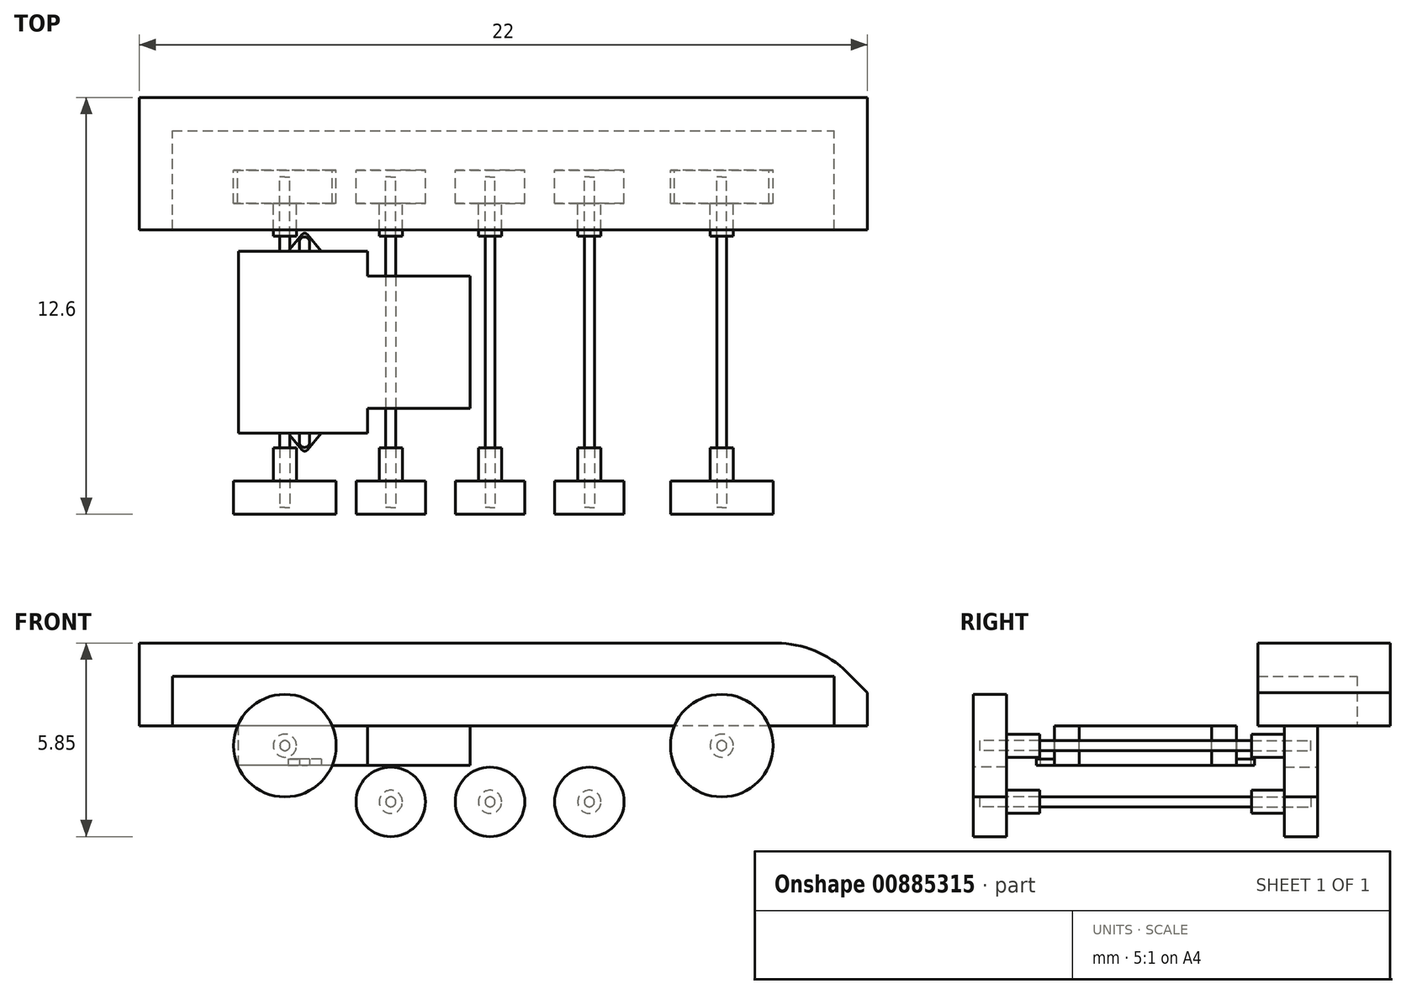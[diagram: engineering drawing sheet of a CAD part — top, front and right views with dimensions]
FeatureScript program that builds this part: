
annotation { "Feature Type Name" : "Feature", "Feature Type Description" : "" }
export const myFeature = defineFeature(function(context is Context, id is Id, definition is map)
    precondition{}
    {
        {
            var Q0;
            Q0=qCreatedBy(makeId("Front.planeOp"),FACE);
            var sketch = newSketch(context, id + "F0", { "sketchPlane" : qUnion([Q0])});
            skCircle(sketch, "E0", {"center": v(-6.6, 0) * mm, "radius": 0.15 * mm});
            skCircle(sketch, "E1", {"center": v(6.6, 0) * mm, "radius": 0.15 * mm});
            skCircle(sketch, "E2", {"center": v(-3.4, -1.7) * mm, "radius": 0.15 * mm});
            skCircle(sketch, "E3", {"center": v(-0.4, -1.7) * mm, "radius": 0.15 * mm});
            skCircle(sketch, "E4", {"center": v(2.6, -1.7) * mm, "radius": 0.15 * mm});
            skSolve(sketch);
        }
        {
            var Q0;
            Q0=makeQuery(id+"F0.imprint","IMPRINT",FACE,{"disambiguationData":[TD([[makeQuery(id+"F0.imprint","IMPRINT",EDGE,{"derivedFrom":sQuery(id+"F0.wireOp",EDGE,"E0")}),1.0]])]});
            var Q1;
            Q1=makeQuery(id+"F0.imprint","IMPRINT",FACE,{"disambiguationData":[TD([[makeQuery(id+"F0.imprint","IMPRINT",EDGE,{"derivedFrom":sQuery(id+"F0.wireOp",EDGE,"E1")}),1.0]])]});
            var Q2;
            Q2=makeQuery(id+"F0.imprint","IMPRINT",FACE,{"disambiguationData":[TD([[makeQuery(id+"F0.imprint","IMPRINT",EDGE,{"derivedFrom":sQuery(id+"F0.wireOp",EDGE,"E2")}),1.0]])]});
            var Q3;
            Q3=makeQuery(id+"F0.imprint","IMPRINT",FACE,{"disambiguationData":[TD([[makeQuery(id+"F0.imprint","IMPRINT",EDGE,{"derivedFrom":sQuery(id+"F0.wireOp",EDGE,"E3")}),1.0]])]});
            var Q4;
            Q4=makeQuery(id+"F0.imprint","IMPRINT",FACE,{"disambiguationData":[TD([[makeQuery(id+"F0.imprint","IMPRINT",EDGE,{"derivedFrom":sQuery(id+"F0.wireOp",EDGE,"E4")}),1.0]])]});
            extrude(context, id + "F1", {"entities" : qUnion([Q0, Q1, Q2, Q3, Q4]), "endBound" : BoundingType.SYMMETRIC, "depth" : 10 * mm, "offsetDistance" : 25 * mm});
        }
        {
            var Q0;
            Q0=makeQuery(id+"F1.opExtrude","CAP_FACE",FACE,{"disambiguationData":[OSD([sQuery(id+"F0.wireOp",EDGE,"E1")])],"isStart":false});
            var sketch = newSketch(context, id + "F2", { "sketchPlane" : qUnion([Q0])});
            skCircle(sketch, "E5", {"center": v(6.6, 0) * mm, "radius": 1.55 * mm});
            skPoint(sketch, "E6", {"position": v(2.6, -1.7) * mm});
            skPoint(sketch, "E7", {"position": v(-0.4, -1.7) * mm});
            skPoint(sketch, "E8", {"position": v(-3.4, -1.7) * mm});
            skPoint(sketch, "E9", {"position": v(-6.6, 0) * mm});
            skCircle(sketch, "E10", {"center": v(-6.6, 0) * mm, "radius": 1.55 * mm});
            skCircle(sketch, "E11", {"center": v(-3.4, -1.7) * mm, "radius": 1.05 * mm});
            skCircle(sketch, "E12", {"center": v(-0.4, -1.7) * mm, "radius": 1.05 * mm});
            skCircle(sketch, "E13", {"center": v(2.6, -1.7) * mm, "radius": 1.05 * mm});
            skSolve(sketch);
        }
        {
            var Q0;
            Q0=makeQuery(id+"F2.imprint","IMPRINT",FACE,{"disambiguationData":[TD([[makeQuery(id+"F2.imprint","IMPRINT",EDGE,{"derivedFrom":sQuery(id+"F2.wireOp",EDGE,"E10")}),1.0]])]});
            var Q1;
            Q1=makeQuery(id+"F2.imprint","IMPRINT",FACE,{"disambiguationData":[TD([[makeQuery(id+"F2.imprint","IMPRINT",EDGE,{"derivedFrom":sQuery(id+"F2.wireOp",EDGE,"E11")}),1.0]])]});
            var Q2;
            Q2=makeQuery(id+"F2.imprint","IMPRINT",FACE,{"disambiguationData":[TD([[makeQuery(id+"F2.imprint","IMPRINT",EDGE,{"derivedFrom":sQuery(id+"F2.wireOp",EDGE,"E12")}),1.0]])]});
            var Q3;
            Q3=makeQuery(id+"F2.imprint","IMPRINT",FACE,{"disambiguationData":[TD([[makeQuery(id+"F2.imprint","IMPRINT",EDGE,{"derivedFrom":sQuery(id+"F2.wireOp",EDGE,"E13")}),1.0]])]});
            var Q4;
            Q4=makeQuery(id+"F2.imprint","IMPRINT",FACE,{"disambiguationData":[TD([[makeQuery(id+"F2.imprint","IMPRINT",EDGE,{"derivedFrom":sQuery(id+"F2.wireOp",EDGE,"E5")}),1.0]])]});
            extrude(context, id + "F3", {"entities" : qUnion([Q0, Q1, Q2, Q3, Q4]), "oppositeDirection" : true, "depth" : .8 * mm, "offsetDistance" : 25 * mm});
        }
        {
            var Q0;
            Q0=makeQuery(id+"F3.opExtrude","CAP_FACE",FACE,{"disambiguationData":[OSD([sQuery(id+"F2.wireOp",EDGE,"E10")])],"isStart":false});
            var sketch = newSketch(context, id + "F4", { "sketchPlane" : qUnion([Q0])});
            skCircle(sketch, "E14", {"center": v(6.6, 0) * mm, "radius": 0.35 * mm});
            skPoint(sketch, "E15", {"position": v(3.4, -1.7) * mm});
            skPoint(sketch, "E16", {"position": v(0.4, -1.7) * mm});
            skPoint(sketch, "E17", {"position": v(-2.6, -1.7) * mm});
            skPoint(sketch, "E18", {"position": v(-6.6, 0) * mm});
            skCircle(sketch, "E19", {"center": v(3.4, -1.7) * mm, "radius": 0.35 * mm});
            skCircle(sketch, "E20", {"center": v(0.4, -1.7) * mm, "radius": 0.35 * mm});
            skCircle(sketch, "E21", {"center": v(-2.6, -1.7) * mm, "radius": 0.35 * mm});
            skCircle(sketch, "E22", {"center": v(-6.6, 0) * mm, "radius": 0.35 * mm});
            skSolve(sketch);
        }
        {
            var Q0;
            Q0=makeQuery(id+"F4.imprint","IMPRINT",FACE,{"disambiguationData":[TD([[makeQuery(id+"F4.imprint","IMPRINT",EDGE,{"derivedFrom":sQuery(id+"F4.wireOp",EDGE,"E22")}),1.0]])]});
            var Q1;
            Q1=makeQuery(id+"F4.imprint","IMPRINT",FACE,{"disambiguationData":[TD([[makeQuery(id+"F4.imprint","IMPRINT",EDGE,{"derivedFrom":sQuery(id+"F4.wireOp",EDGE,"E21")}),1.0]])]});
            var Q2;
            Q2=makeQuery(id+"F4.imprint","IMPRINT",FACE,{"disambiguationData":[TD([[makeQuery(id+"F4.imprint","IMPRINT",EDGE,{"derivedFrom":sQuery(id+"F4.wireOp",EDGE,"E20")}),1.0]])]});
            var Q3;
            Q3=makeQuery(id+"F4.imprint","IMPRINT",FACE,{"disambiguationData":[TD([[makeQuery(id+"F4.imprint","IMPRINT",EDGE,{"derivedFrom":sQuery(id+"F4.wireOp",EDGE,"E19")}),1.0]])]});
            var Q4;
            Q4=makeQuery(id+"F4.imprint","IMPRINT",FACE,{"disambiguationData":[TD([[makeQuery(id+"F4.imprint","IMPRINT",EDGE,{"derivedFrom":sQuery(id+"F4.wireOp",EDGE,"E14")}),1.0]])]});
            extrude(context, id + "F5", {"entities" : qUnion([Q0, Q1, Q2, Q3, Q4]), "operationType" : NewBodyOperationType.ADD, "depth" : 1 * mm, "offsetDistance" : 25 * mm});
        }
        {
            var Q0;
            Q0=qCreatedBy(makeId("Top.planeOp"),FACE);
            var sketch = newSketch(context, id + "F6", { "sketchPlane" : qUnion([Q0])});
            skLineSegment(sketch, "E23.bottom", {"start": v(-4.1, 2.75) * mm, "end": v(-8, 2.75) * mm});
            skLineSegment(sketch, "E23.top", {"start": v(-4.1, -2.75) * mm, "end": v(-8, -2.75) * mm});
            skLineSegment(sketch, "E23.left", {"start": v(-4.1, 2.75) * mm, "end": v(-4.1, -2.75) * mm});
            skLineSegment(sketch, "E23.right", {"start": v(-8, 2.75) * mm, "end": v(-8, -2.75) * mm});
            skPoint(sketch, "E23.middle", {"position": v(-6.05, 0) * mm});
            skLineSegment(sketch, "E24.bottom", {"start": v(-4.1, -2) * mm, "end": v(-1, -2) * mm});
            skLineSegment(sketch, "E24.top", {"start": v(-4.1, 2) * mm, "end": v(-1, 2) * mm});
            skLineSegment(sketch, "E24.left", {"start": v(-4.1, -2) * mm, "end": v(-4.1, 2) * mm});
            skLineSegment(sketch, "E24.right", {"start": v(-1, -2) * mm, "end": v(-1, 2) * mm});
            skSolve(sketch);
        }
        {
            var Q0;
            Q0 = qSketchRegion(id + "F6", true);
            extrude(context, id + "F7", {"entities" : qUnion([Q0]), "operationType" : NewBodyOperationType.ADD, "endBound" : BoundingType.SYMMETRIC, "oppositeDirection" : true, "depth" : 1.2 * mm, "offsetDistance" : 25 * mm});
        }
        {
            var Q0;
            Q0=makeQuery(id+"F7.opExtrude","CAP_FACE",FACE,{"disambiguationData":[OSD([sQuery(id+"F6.wireOp",EDGE,"E23.bottom"),sQuery(id+"F6.wireOp",EDGE,"E23.top"),sQuery(id+"F6.wireOp",EDGE,"E23.left"),sQuery(id+"F6.wireOp",EDGE,"E23.right"),sQuery(id+"F6.wireOp",EDGE,"E24.bottom"),sQuery(id+"F6.wireOp",EDGE,"E24.top"),sQuery(id+"F6.wireOp",EDGE,"E24.right")])],"isStart":false});
            var sketch = newSketch(context, id + "F8", { "sketchPlane" : qUnion([Q0])});
            skPoint(sketch, "E25", {"position": v(-6.5, 2.75) * mm});
            skPoint(sketch, "E26", {"position": v(-5.5, 2.75) * mm});
            skPoint(sketch, "E27", {"position": v(-6, 2.75) * mm});
            skPoint(sketch, "E28", {"position": v(-6, 3.35) * mm});
            skLineSegment(sketch, "E29", {"start": v(-6.5, 2.75) * mm, "end": v(-6, 3.35) * mm});
            skLineSegment(sketch, "E30", {"start": v(-5.5, 2.75) * mm, "end": v(-6, 3.35) * mm});
            skCircle(sketch, "E31", {"center": v(-6, 3.03) * mm, "radius": 0.15 * mm});
            skLineSegment(sketch, "E32", {"start": v(-6.16, 3.03) * mm, "end": v(-6.16, 2.75) * mm});
            skLineSegment(sketch, "E33", {"start": v(-5.86, 3.03) * mm, "end": v(-5.86, 2.75) * mm});
            skSolve(sketch);
        }
        {
            var Q0;
            {var subQ1=sQuery(id+"F8.wireOp",EDGE,"E29");Q0=makeQuery(id+"F8.imprint","IMPRINT",FACE,{"disambiguationData":[TD([[makeQuery(id+"F8.imprint","IMPRINT",EDGE,{"derivedFrom":subQ1}),-1.0]])]});}
            extrude(context, id + "F9", {"entities" : qUnion([Q0]), "operationType" : NewBodyOperationType.ADD, "oppositeDirection" : true, "depth" : .2 * mm, "offsetDistance" : 25 * mm});
        }
        {
            var Q0;
            Q0=makeQuery(id+"F9.opExtrude","SWEPT_EDGE",EDGE,{"disambiguationData":[OSD([sQuery(id+"F8.wireOp",EDGE,"E29"),sQuery(id+"F8.wireOp",EDGE,"E30")])]});
            fillet(context, id + "F10", {"entities" : qUnion([Q0]), "radius" : .1 * mm, "tangentPropagation" : true, "allowEdgeOverflow" : false});
        }
        {
            var Q0;
            Q0=makeQuery(id+"F3.opExtrude","CAP_FACE",FACE,{"disambiguationData":[OSD([sQuery(id+"F0.wireOp",EDGE,"E1"),sQuery(id+"F2.wireOp",EDGE,"E5")])],"isStart":true});
            var Q1;
            Q1=makeQuery(id+"F3.opExtrude","CAP_FACE",FACE,{"disambiguationData":[OSD([sQuery(id+"F2.wireOp",EDGE,"E13")])],"isStart":true});
            var Q2;
            Q2=makeQuery(id+"F3.opExtrude","CAP_FACE",FACE,{"disambiguationData":[OSD([sQuery(id+"F2.wireOp",EDGE,"E12")])],"isStart":true});
            var Q3;
            Q3=makeQuery(id+"F3.opExtrude","CAP_FACE",FACE,{"disambiguationData":[OSD([sQuery(id+"F2.wireOp",EDGE,"E11")])],"isStart":true});
            var Q4;
            Q4=makeQuery(id+"F3.opExtrude","CAP_FACE",FACE,{"disambiguationData":[OSD([sQuery(id+"F2.wireOp",EDGE,"E10")])],"isStart":true});
            extrude(context, id + "F11", {"entities" : qUnion([Q0, Q1, Q2, Q3, Q4]), "operationType" : NewBodyOperationType.ADD, "depth" : .2 * mm, "offsetDistance" : 25 * mm});
        }
        {
            var Q0;
            Q0=makeQuery(id+"F1.opExtrude","SWEPT_BODY",BODY,{"disambiguationData":[OSD([sQuery(id+"F0.wireOp",EDGE,"E0")])]});
            var Q1;
            Q1=makeQuery(id+"F1.opExtrude","SWEPT_BODY",BODY,{"disambiguationData":[OSD([sQuery(id+"F0.wireOp",EDGE,"E1")])]});
            var Q2;
            Q2=makeQuery(id+"F1.opExtrude","SWEPT_BODY",BODY,{"disambiguationData":[OSD([sQuery(id+"F0.wireOp",EDGE,"E2")])]});
            var Q3;
            Q3=makeQuery(id+"F1.opExtrude","SWEPT_BODY",BODY,{"disambiguationData":[OSD([sQuery(id+"F0.wireOp",EDGE,"E3")])]});
            var Q4;
            Q4=makeQuery(id+"F1.opExtrude","SWEPT_BODY",BODY,{"disambiguationData":[OSD([sQuery(id+"F0.wireOp",EDGE,"E4")])]});
            var Q5;
            Q5=makeQuery(id+"F3.opExtrude","SWEPT_BODY",BODY,{"disambiguationData":[OSD([sQuery(id+"F2.wireOp",EDGE,"E11")])]});
            var Q6;
            Q6=makeQuery(id+"F3.opExtrude","SWEPT_BODY",BODY,{"disambiguationData":[OSD([sQuery(id+"F2.wireOp",EDGE,"E12")])]});
            var Q7;
            Q7=makeQuery(id+"F3.opExtrude","SWEPT_BODY",BODY,{"disambiguationData":[OSD([sQuery(id+"F2.wireOp",EDGE,"E10")])]});
            var Q8;
            Q8=makeQuery(id+"F3.opExtrude","SWEPT_BODY",BODY,{"disambiguationData":[OSD([sQuery(id+"F0.wireOp",EDGE,"E1"),sQuery(id+"F2.wireOp",EDGE,"E5")])]});
            var Q9;
            Q9=makeQuery(id+"F3.opExtrude","SWEPT_BODY",BODY,{"disambiguationData":[OSD([sQuery(id+"F2.wireOp",EDGE,"E13")])]});
            var Q10;
            Q10=qCreatedBy(makeId("Front.planeOp"),FACE);
            mirror(context, id + "F12", {"entities" : qUnion([Q0, Q1, Q2, Q3, Q4, Q5, Q6, Q7, Q8, Q9]), "mirrorPlane" : qUnion([Q10])});
        }
        {
            var Q0;
            Q0=makeQuery(id+"F7.opExtrude","CAP_FACE",FACE,{"disambiguationData":[OSD([sQuery(id+"F6.wireOp",EDGE,"E23.bottom"),sQuery(id+"F6.wireOp",EDGE,"E23.top"),sQuery(id+"F6.wireOp",EDGE,"E23.left"),sQuery(id+"F6.wireOp",EDGE,"E23.right"),sQuery(id+"F6.wireOp",EDGE,"E24.bottom"),sQuery(id+"F6.wireOp",EDGE,"E24.top"),sQuery(id+"F6.wireOp",EDGE,"E24.right")])],"isStart":true});
            var sketch = newSketch(context, id + "F13", { "sketchPlane" : qUnion([Q0])});
            skLineSegment(sketch, "E34.bottom", {"start": v(-11, 7.4) * mm, "end": v(11, 7.4) * mm});
            skLineSegment(sketch, "E34.top", {"start": v(-11, 3.4) * mm, "end": v(11, 3.4) * mm});
            skLineSegment(sketch, "E34.left", {"start": v(-11, 7.4) * mm, "end": v(-11, 3.4) * mm});
            skLineSegment(sketch, "E34.right", {"start": v(11, 7.4) * mm, "end": v(11, 3.4) * mm});
            skLineSegment(sketch, "E35.bottom", {"start": v(11, 3.4) * mm, "end": v(9.5, 3.4) * mm});
            skLineSegment(sketch, "E35.top", {"start": v(11, 0) * mm, "end": v(9.5, 0) * mm});
            skLineSegment(sketch, "E35.left", {"start": v(11, 3.4) * mm, "end": v(11, 0) * mm});
            skLineSegment(sketch, "E35.right", {"start": v(9.5, 3.4) * mm, "end": v(9.5, 0) * mm});
            skSolve(sketch);
        }
        {
            var Q0;
            Q0=makeQuery(id+"F13.imprint","IMPRINT",FACE,{"disambiguationData":[TD([[makeQuery(id+"F13.imprint","IMPRINT",EDGE,{"derivedFrom":sQuery(id+"F13.wireOp",EDGE,"E34.bottom")}),-1.0]])]});
            var Q1;
            Q1=makeQuery(id+"F13.imprint","IMPRINT",FACE,{"disambiguationData":[TD([[makeQuery(id+"F13.imprint","IMPRINT",EDGE,{"derivedFrom":sQuery(id+"F13.wireOp",EDGE,"E35.bottom")}),1.0]])]});
            extrude(context, id + "F14", {"entities" : qUnion([Q0, Q1]), "depth" : 2.5 * mm, "offsetDistance" : 25 * mm});
        }
        {
            var Q0;
            Q0=makeQuery(id+"F14.opExtrude","CAP_EDGE",EDGE,{"disambiguationData":[OSD([sQuery(id+"F13.wireOp",EDGE,"E34.right"),sQuery(id+"F13.wireOp",EDGE,"E35.left")])],"isStart":false});
            chamfer(context, id + "F15", {"entities" : qUnion([Q0]), "width" : 1.5 * mm, "tangentPropagation" : true});
        }
        {
            var Q0;
            {var subQ0=sQuery(id+"F13.wireOp",EDGE,"E35.left");var subQ1=sQuery(id+"F13.wireOp",EDGE,"E34.right");Q0=makeQuery(id+"F15.opChamfer","BLEND_EDGE",EDGE,{"blendedFrom":[makeQuery(id+"F14.opExtrude","CAP_EDGE",EDGE,{"disambiguationData":[OSD([subQ1,subQ0])],"isStart":false}),makeQuery(id+"F14.opExtrude","CAP_FACE",FACE,{"disambiguationData":[OSD([sQuery(id+"F13.wireOp",EDGE,"E34.bottom"),sQuery(id+"F13.wireOp",EDGE,"E34.top"),sQuery(id+"F13.wireOp",EDGE,"E34.left"),subQ1,sQuery(id+"F13.wireOp",EDGE,"E35.top"),subQ0,sQuery(id+"F13.wireOp",EDGE,"E35.right")])],"isStart":false})],"blendedInto":[makeQuery(id+"F14.opExtrude","CAP_FACE",FACE,{"disambiguationData":[OSD([sQuery(id+"F13.wireOp",EDGE,"E34.bottom"),sQuery(id+"F13.wireOp",EDGE,"E34.top"),sQuery(id+"F13.wireOp",EDGE,"E34.left"),subQ1,sQuery(id+"F13.wireOp",EDGE,"E35.top"),subQ0,sQuery(id+"F13.wireOp",EDGE,"E35.right")])],"isStart":false})]});}
            fillet(context, id + "F16", {"entities" : qUnion([Q0]), "radius" : 3 * mm, "tangentPropagation" : true, "allowEdgeOverflow" : false});
        }
        {
            var Q0;
            Q0=makeQuery(id+"F14.opExtrude","CAP_FACE",FACE,{"disambiguationData":[OSD([sQuery(id+"F13.wireOp",EDGE,"E34.bottom"),sQuery(id+"F13.wireOp",EDGE,"E34.top"),sQuery(id+"F13.wireOp",EDGE,"E34.left"),sQuery(id+"F13.wireOp",EDGE,"E34.right"),sQuery(id+"F13.wireOp",EDGE,"E35.top"),sQuery(id+"F13.wireOp",EDGE,"E35.left"),sQuery(id+"F13.wireOp",EDGE,"E35.right")])],"isStart":true});
            var sketch = newSketch(context, id + "F17", { "sketchPlane" : qUnion([Q0])});
            skLineSegment(sketch, "E36.bottom", {"start": v(-10, -3.4) * mm, "end": v(10, -3.4) * mm});
            skLineSegment(sketch, "E36.top", {"start": v(-10, -6.4) * mm, "end": v(10, -6.4) * mm});
            skLineSegment(sketch, "E36.left", {"start": v(-10, -3.4) * mm, "end": v(-10, -6.4) * mm});
            skLineSegment(sketch, "E36.right", {"start": v(10, -3.4) * mm, "end": v(10, -6.4) * mm});
            skSolve(sketch);
        }
        {
            var Q0;
            Q0=makeQuery(id+"F17.imprint","IMPRINT",FACE,{"disambiguationData":[TD([[makeQuery(id+"F17.imprint","IMPRINT",EDGE,{"derivedFrom":sQuery(id+"F17.wireOp",EDGE,"E36.top")}),1.0]])]});
            extrude(context, id + "F18", {"entities" : qUnion([Q0]), "operationType" : NewBodyOperationType.REMOVE, "oppositeDirection" : true, "depth" : 1.5 * mm, "offsetDistance" : 25 * mm});
        }
    });
